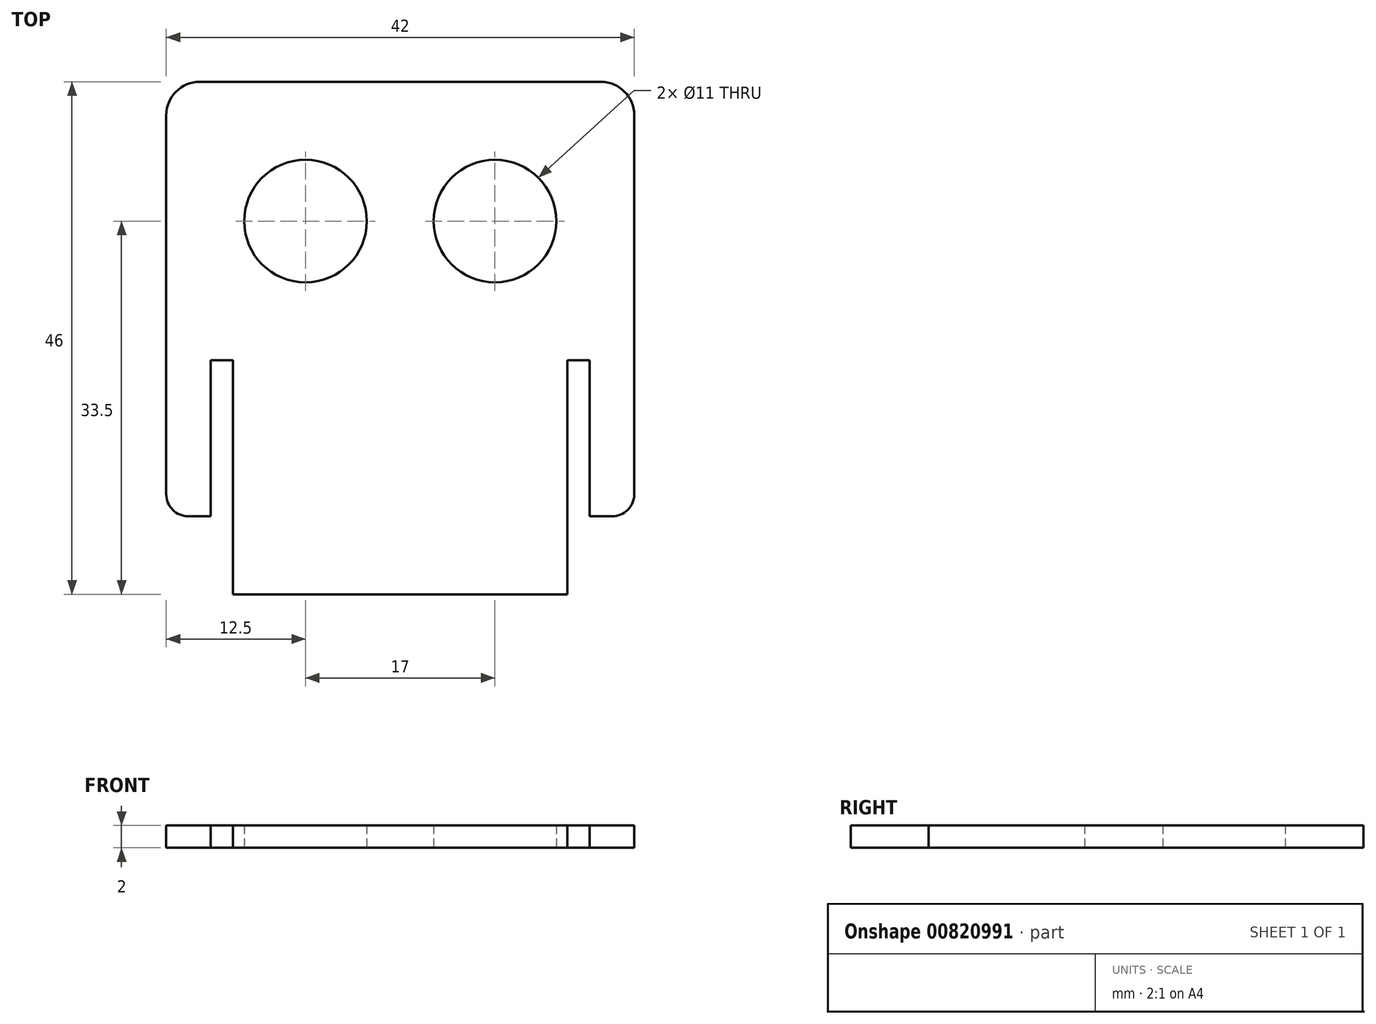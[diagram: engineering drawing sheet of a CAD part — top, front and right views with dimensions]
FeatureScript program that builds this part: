
annotation { "Feature Type Name" : "Feature", "Feature Type Description" : "" }
export const myFeature = defineFeature(function(context is Context, id is Id, definition is map)
    precondition{}
    {
        {
            var Q0;
            Q0=qCreatedBy(makeId("Top.planeOp"),FACE);
            var sketch = newSketch(context, id + "F0", { "sketchPlane" : qUnion([Q0])});
            skLineSegment(sketch, "E0.bottom", {"start": v(-15, 23) * mm, "end": v(15, 23) * mm});
            skLineSegment(sketch, "E0.top", {"start": v(-15, -23) * mm, "end": v(15, -23) * mm});
            skLineSegment(sketch, "E0.left", {"start": v(-15, -2) * mm, "end": v(-15, -23) * mm});
            skLineSegment(sketch, "E0.right", {"start": v(15, -2) * mm, "end": v(15, -23) * mm});
            skPoint(sketch, "E0.middle", {"position": v(0, 0) * mm});
            skLineSegment(sketch, "E1", {"start": v(-17, -16) * mm, "end": v(-19, -16) * mm});
            skLineSegment(sketch, "E2", {"start": v(-15, 23) * mm, "end": v(-18, 23) * mm});
            skLineSegment(sketch, "E3", {"start": v(-21, 20) * mm, "end": v(-21, -14) * mm});
            skLineSegment(sketch, "E4", {"start": v(-17, -2) * mm, "end": v(-15, -2) * mm});
            skLineSegment(sketch, "E5", {"start": v(-17, -2) * mm, "end": v(-17, -16) * mm});
            skPoint(sketch, "E6.visualSharp", {"position": v(-21, 23) * mm});
            skArc(sketch, "E6.filletArc", {"start": v(-18, 23) * mm, "mid": v(-20.12, 22.12) * mm, "end": v(-21, 20) * mm});
            skPoint(sketch, "E7.visualSharp", {"position": v(-21, -16) * mm});
            skArc(sketch, "E7.filletArc", {"start": v(-21, -14) * mm, "mid": v(-20.41, -15.41) * mm, "end": v(-19, -16) * mm});
            skCircle(sketch, "E8", {"center": v(-8.5, 10.5) * mm, "radius": 5.5 * mm});
            skCircle(sketch, "E9.MirrorC", {"center": v(8.5, 10.5) * mm, "radius": 5.5 * mm});
            skLineSegment(sketch, "E10.MirrorCS", {"start": v(15, 23) * mm, "end": v(18, 23) * mm});
            skArc(sketch, "E11.MirrorCS", {"start": v(18, 23) * mm, "mid": v(20.12, 22.12) * mm, "end": v(21, 20) * mm});
            skLineSegment(sketch, "E12.MirrorCS", {"start": v(21, 20) * mm, "end": v(21, -14) * mm});
            skArc(sketch, "E13.MirrorCS", {"start": v(21, -14) * mm, "mid": v(20.41, -15.41) * mm, "end": v(19, -16) * mm});
            skLineSegment(sketch, "E14.MirrorCS", {"start": v(17, -16) * mm, "end": v(19, -16) * mm});
            skLineSegment(sketch, "E15.MirrorCS", {"start": v(17, -2) * mm, "end": v(17, -16) * mm});
            skLineSegment(sketch, "E16.MirrorCS", {"start": v(17, -2) * mm, "end": v(15, -2) * mm});
            skSolve(sketch);
        }
        {
            var Q0;
            Q0 = qSketchRegion(id + "F0", true);
            extrude(context, id + "F1", {"entities" : qUnion([Q0]), "depth" : 2 * mm, "offsetDistance" : 25 * mm});
        }
    });
